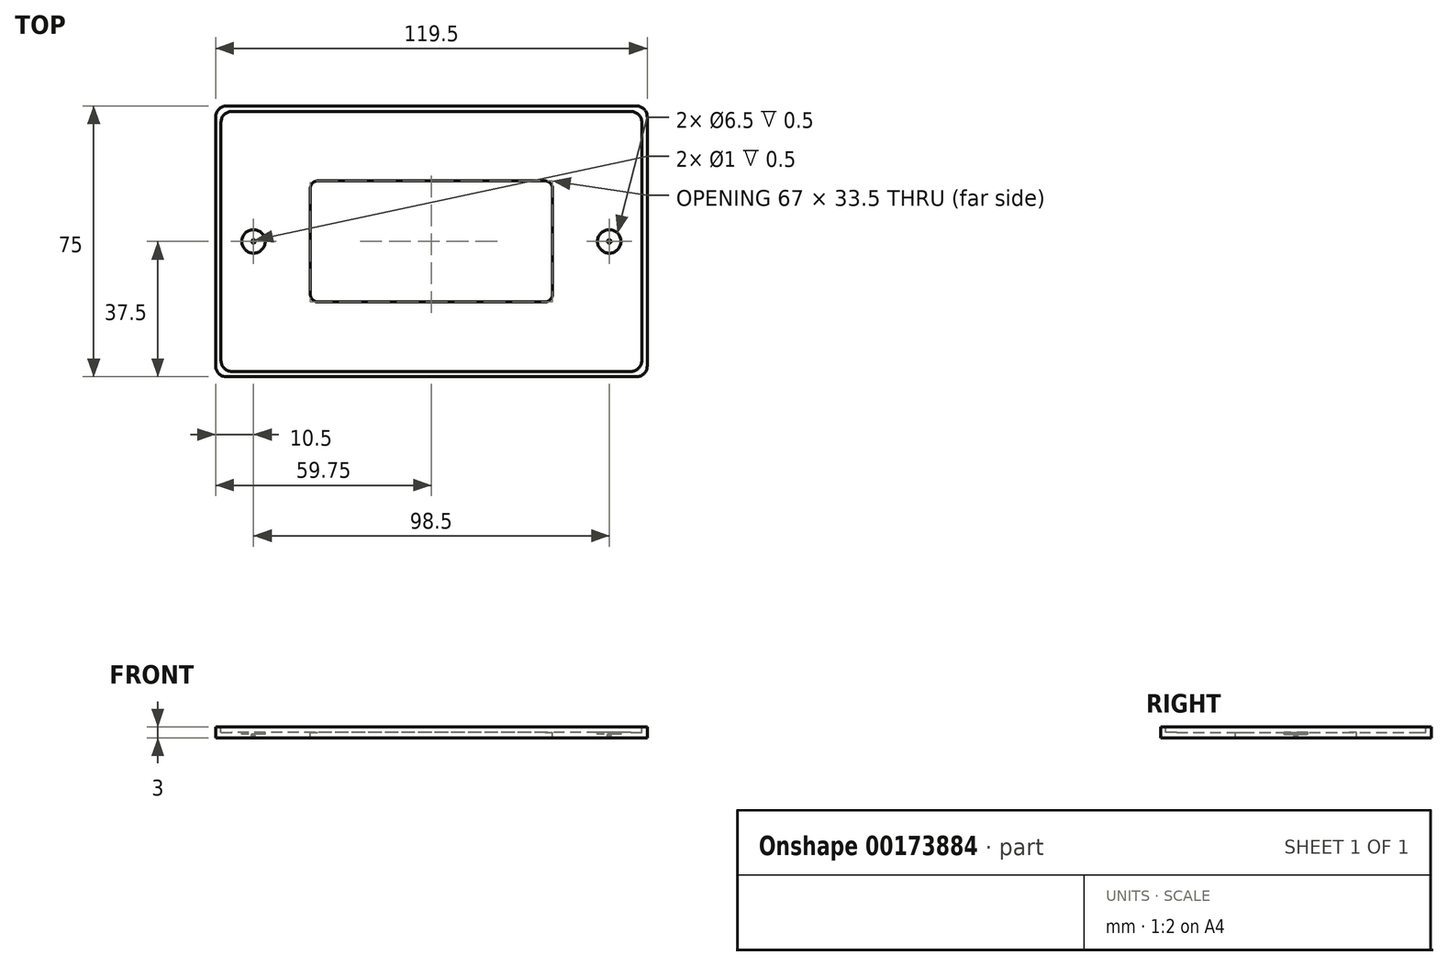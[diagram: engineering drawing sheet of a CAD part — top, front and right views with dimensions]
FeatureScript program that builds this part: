
annotation { "Feature Type Name" : "Feature", "Feature Type Description" : "" }
export const myFeature = defineFeature(function(context is Context, id is Id, definition is map)
    precondition{}
    {
        {
            var Q0;
            Q0=qCreatedBy(makeId("Top.planeOp"),FACE);
            var sketch = newSketch(context, id + "F0", { "sketchPlane" : qUnion([Q0])});
            skLineSegment(sketch, "E0.bottom", {"start": v(56.75, -37.5) * mm, "end": v(-56.75, -37.5) * mm});
            skLineSegment(sketch, "E0.top", {"start": v(56.75, 37.5) * mm, "end": v(-56.75, 37.5) * mm});
            skLineSegment(sketch, "E0.left", {"start": v(59.75, -34.5) * mm, "end": v(59.75, 34.5) * mm});
            skLineSegment(sketch, "E0.right", {"start": v(-59.75, -34.5) * mm, "end": v(-59.75, 34.5) * mm});
            skPoint(sketch, "E0.middle", {"position": v(0, 0) * mm});
            skPoint(sketch, "E1.visualSharp", {"position": v(-59.75, 37.5) * mm});
            skArc(sketch, "E1.filletArc", {"start": v(-56.75, 37.5) * mm, "mid": v(-58.87, 36.62) * mm, "end": v(-59.75, 34.5) * mm});
            skPoint(sketch, "E2.visualSharp", {"position": v(-59.75, -37.5) * mm});
            skArc(sketch, "E2.filletArc", {"start": v(-59.75, -34.5) * mm, "mid": v(-58.87, -36.62) * mm, "end": v(-56.75, -37.5) * mm});
            skPoint(sketch, "E3.visualSharp", {"position": v(59.75, 37.5) * mm});
            skArc(sketch, "E3.filletArc", {"start": v(59.75, 34.5) * mm, "mid": v(58.87, 36.62) * mm, "end": v(56.75, 37.5) * mm});
            skPoint(sketch, "E4.visualSharp", {"position": v(59.75, -37.5) * mm});
            skArc(sketch, "E4.filletArc", {"start": v(56.75, -37.5) * mm, "mid": v(58.87, -36.62) * mm, "end": v(59.75, -34.5) * mm});
            skSolve(sketch);
        }
        {
            var Q0;
            Q0 = qSketchRegion(id + "F0", true);
            extrude(context, id + "F1", {"entities" : qUnion([Q0]), "depth" : 3 * mm});
        }
        {
            var Q0;
            Q0=makeQuery(id+"F1.opExtrude","CAP_FACE",FACE,{"disambiguationData":[OSD([sQuery(id+"F0.wireOp",EDGE,"E0.bottom"),sQuery(id+"F0.wireOp",EDGE,"E0.top"),sQuery(id+"F0.wireOp",EDGE,"E0.left"),sQuery(id+"F0.wireOp",EDGE,"E0.right"),sQuery(id+"F0.wireOp",EDGE,"E1.filletArc"),sQuery(id+"F0.wireOp",EDGE,"E2.filletArc"),sQuery(id+"F0.wireOp",EDGE,"E3.filletArc"),sQuery(id+"F0.wireOp",EDGE,"E4.filletArc")])],"isStart":false});
            var sketch = newSketch(context, id + "F2", { "sketchPlane" : qUnion([Q0])});
            skLineSegment(sketch, "E5.0", {"start": v(55.25, 36) * mm, "end": v(-55.25, 36) * mm});
            skLineSegment(sketch, "E5.1", {"start": v(58.25, -33) * mm, "end": v(58.25, 33) * mm});
            skLineSegment(sketch, "E5.2", {"start": v(55.25, -36) * mm, "end": v(-55.25, -36) * mm});
            skLineSegment(sketch, "E5.3", {"start": v(-58.25, -33) * mm, "end": v(-58.25, 33) * mm});
            skPoint(sketch, "E6.visualSharp", {"position": v(-58.25, 36) * mm});
            skArc(sketch, "E6.filletArc", {"start": v(-55.25, 36) * mm, "mid": v(-57.37, 35.12) * mm, "end": v(-58.25, 33) * mm});
            skPoint(sketch, "E7.visualSharp", {"position": v(-58.25, -36) * mm});
            skArc(sketch, "E7.filletArc", {"start": v(-58.25, -33) * mm, "mid": v(-57.37, -35.12) * mm, "end": v(-55.25, -36) * mm});
            skPoint(sketch, "E8.visualSharp", {"position": v(58.25, -36) * mm});
            skArc(sketch, "E8.filletArc", {"start": v(55.25, -36) * mm, "mid": v(57.37, -35.12) * mm, "end": v(58.25, -33) * mm});
            skPoint(sketch, "E9.visualSharp", {"position": v(58.25, 36) * mm});
            skArc(sketch, "E9.filletArc", {"start": v(58.25, 33) * mm, "mid": v(57.37, 35.12) * mm, "end": v(55.25, 36) * mm});
            skSolve(sketch);
        }
        {
            var Q0;
            Q0 = qSketchRegion(id + "F2", true);
            extrude(context, id + "F3", {"entities" : qUnion([Q0]), "operationType" : NewBodyOperationType.REMOVE, "oppositeDirection" : true, "depth" : 1.5 * mm});
        }
        {
            var Q0;
            Q0=makeQuery(id+"F3.boolean.opBoolean","COPY",FACE,{"derivedFrom":makeQuery(id+"F3.opExtrude","CAP_FACE",FACE,{"disambiguationData":[OSD([sQuery(id+"F2.wireOp",EDGE,"E5.0"),sQuery(id+"F2.wireOp",EDGE,"E5.1"),sQuery(id+"F2.wireOp",EDGE,"E5.2"),sQuery(id+"F2.wireOp",EDGE,"E5.3"),sQuery(id+"F2.wireOp",EDGE,"E6.filletArc"),sQuery(id+"F2.wireOp",EDGE,"E7.filletArc"),sQuery(id+"F2.wireOp",EDGE,"E8.filletArc"),sQuery(id+"F2.wireOp",EDGE,"E9.filletArc")])],"isStart":false})});
            var sketch = newSketch(context, id + "F4", { "sketchPlane" : qUnion([Q0])});
            skLineSegment(sketch, "E10.bottom", {"start": v(31.5, -16.75) * mm, "end": v(-31.5, -16.75) * mm});
            skLineSegment(sketch, "E10.top", {"start": v(31.5, 16.75) * mm, "end": v(-31.5, 16.75) * mm});
            skLineSegment(sketch, "E10.left", {"start": v(33.5, -14.75) * mm, "end": v(33.5, 14.75) * mm});
            skLineSegment(sketch, "E10.right", {"start": v(-33.5, -14.75) * mm, "end": v(-33.5, 14.75) * mm});
            skPoint(sketch, "E10.middle", {"position": v(0, 0) * mm});
            skPoint(sketch, "E11.visualSharp", {"position": v(-33.5, 16.75) * mm});
            skArc(sketch, "E11.filletArc", {"start": v(-31.5, 16.75) * mm, "mid": v(-32.91, 16.16) * mm, "end": v(-33.5, 14.75) * mm});
            skPoint(sketch, "E12.visualSharp", {"position": v(33.5, 16.75) * mm});
            skArc(sketch, "E12.filletArc", {"start": v(33.5, 14.75) * mm, "mid": v(32.91, 16.16) * mm, "end": v(31.5, 16.75) * mm});
            skPoint(sketch, "E13.visualSharp", {"position": v(33.5, -16.75) * mm});
            skArc(sketch, "E13.filletArc", {"start": v(31.5, -16.75) * mm, "mid": v(32.91, -16.16) * mm, "end": v(33.5, -14.75) * mm});
            skPoint(sketch, "E14.visualSharp", {"position": v(-33.5, -16.75) * mm});
            skArc(sketch, "E14.filletArc", {"start": v(-33.5, -14.75) * mm, "mid": v(-32.91, -16.16) * mm, "end": v(-31.5, -16.75) * mm});
            skSolve(sketch);
        }
        {
            var Q0;
            Q0 = qSketchRegion(id + "F4", true);
            extrude(context, id + "F5", {"entities" : qUnion([Q0]), "operationType" : NewBodyOperationType.REMOVE, "endBound" : BoundingType.THROUGH_ALL, "oppositeDirection" : true, "depth" : 25 * mm});
        }
        {
            var Q0;
            Q0=makeQuery(id+"F3.boolean.opBoolean","COPY",FACE,{"derivedFrom":makeQuery(id+"F3.opExtrude","CAP_FACE",FACE,{"disambiguationData":[OSD([sQuery(id+"F2.wireOp",EDGE,"E5.0"),sQuery(id+"F2.wireOp",EDGE,"E5.1"),sQuery(id+"F2.wireOp",EDGE,"E5.2"),sQuery(id+"F2.wireOp",EDGE,"E5.3"),sQuery(id+"F2.wireOp",EDGE,"E6.filletArc"),sQuery(id+"F2.wireOp",EDGE,"E7.filletArc"),sQuery(id+"F2.wireOp",EDGE,"E8.filletArc"),sQuery(id+"F2.wireOp",EDGE,"E9.filletArc")])],"isStart":false})});
            var sketch = newSketch(context, id + "F6", { "sketchPlane" : qUnion([Q0])});
            skCircle(sketch, "E15", {"center": v(49.25, 0) * mm, "radius": 3.25 * mm});
            skCircle(sketch, "E16.MirrorC", {"center": v(-49.25, 0) * mm, "radius": 3.25 * mm});
            skSolve(sketch);
        }
        {
            var Q0;
            Q0 = qSketchRegion(id + "F6", true);
            extrude(context, id + "F7", {"entities" : qUnion([Q0]), "operationType" : NewBodyOperationType.REMOVE, "oppositeDirection" : true, "depth" : .5 * mm});
        }
        {
            var Q0;
            Q0=makeQuery(id+"F7.boolean.opBoolean","COPY",FACE,{"derivedFrom":makeQuery(id+"F7.opExtrude","CAP_FACE",FACE,{"disambiguationData":[OSD([sQuery(id+"F6.wireOp",EDGE,"E16.MirrorC")])],"isStart":false})});
            var sketch = newSketch(context, id + "F8", { "sketchPlane" : qUnion([Q0])});
            skCircle(sketch, "E17", {"center": v(49.25, 0) * mm, "radius": 0.5 * mm});
            skCircle(sketch, "E18.MirrorC", {"center": v(-49.25, 0) * mm, "radius": 0.5 * mm});
            skSolve(sketch);
        }
        {
            var Q0;
            Q0 = qSketchRegion(id + "F8", true);
            extrude(context, id + "F9", {"entities" : qUnion([Q0]), "operationType" : NewBodyOperationType.REMOVE, "oppositeDirection" : true, "depth" : .5 * mm});
        }
    });
